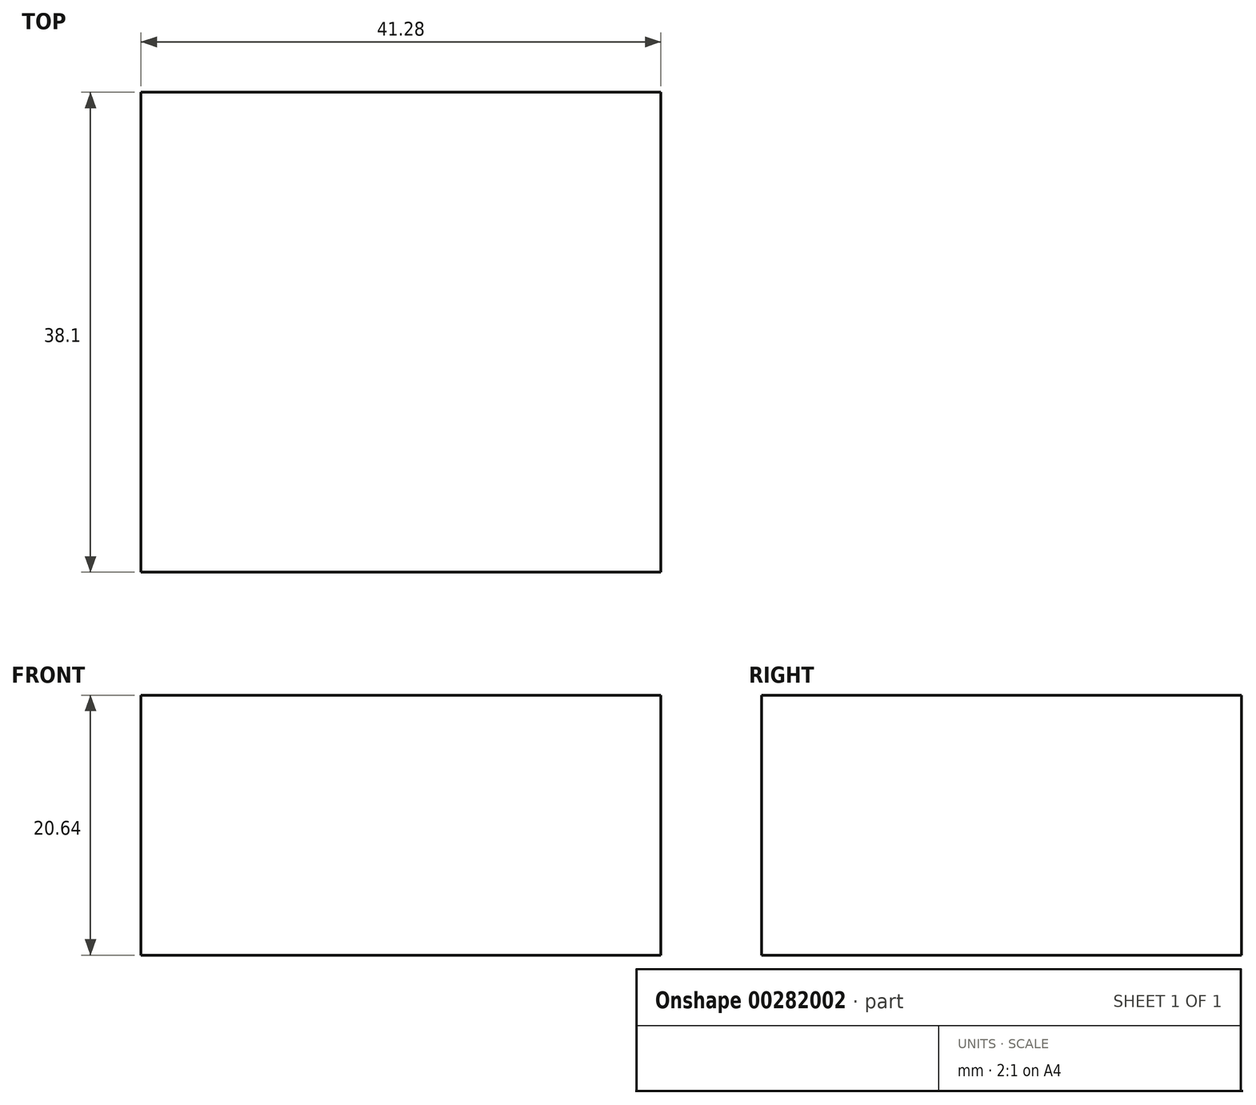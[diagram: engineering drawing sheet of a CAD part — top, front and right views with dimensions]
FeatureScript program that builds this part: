
annotation { "Feature Type Name" : "Feature", "Feature Type Description" : "" }
export const myFeature = defineFeature(function(context is Context, id is Id, definition is map)
    precondition{}
    {
        {
            var Q0;
            Q0=qCreatedBy(makeId("Top.planeOp"),FACE);
            var sketch = newSketch(context, id + "F0", { "sketchPlane" : qUnion([Q0])});
            skLineSegment(sketch, "E0.bottom", {"start": v(-20.64, 27.51) * mm, "end": v(20.64, 27.51) * mm});
            skLineSegment(sketch, "E0.top", {"start": v(-20.64, -10.59) * mm, "end": v(20.64, -10.59) * mm});
            skLineSegment(sketch, "E0.left", {"start": v(-20.64, 27.51) * mm, "end": v(-20.64, -10.59) * mm});
            skLineSegment(sketch, "E0.right", {"start": v(20.64, 27.51) * mm, "end": v(20.64, -10.59) * mm});
            skSolve(sketch);
        }
        {
            var Q0;
            Q0=makeQuery(id+"F0.imprint","IMPRINT",FACE,{"disambiguationData":[TD([[makeQuery(id+"F0.imprint","IMPRINT",EDGE,{"derivedFrom":sQuery(id+"F0.wireOp",EDGE,"E0.bottom")}),-1.0]])]});
            extrude(context, id + "F1", {"entities" : qUnion([Q0]), "depth" : 20.64 * mm});
        }
    });
